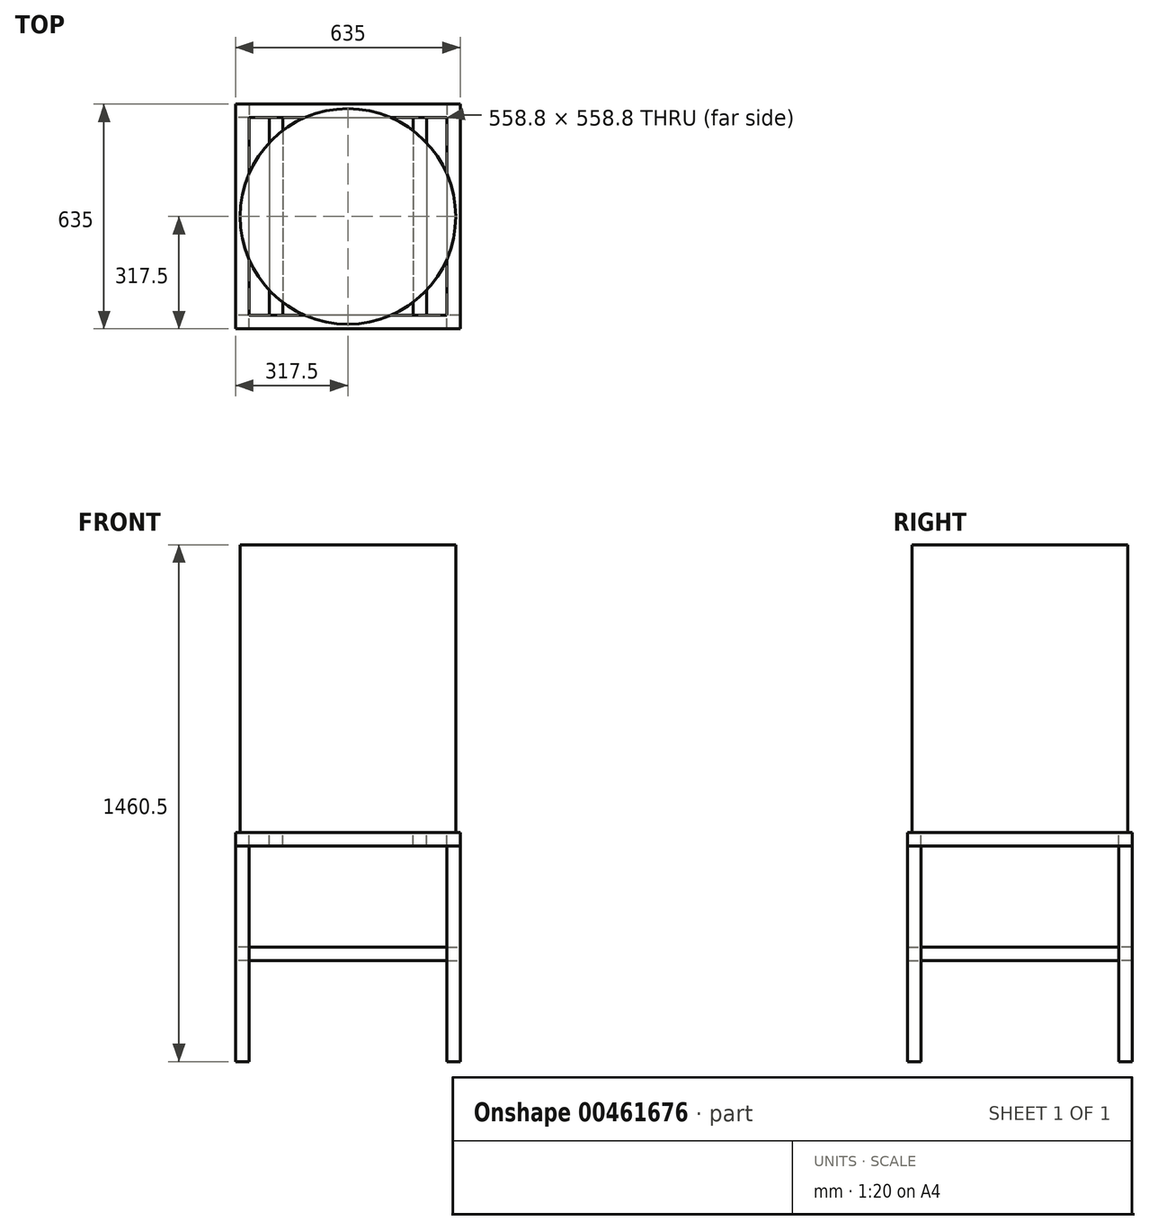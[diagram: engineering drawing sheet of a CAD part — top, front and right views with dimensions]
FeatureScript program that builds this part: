
annotation { "Feature Type Name" : "Feature", "Feature Type Description" : "" }
export const myFeature = defineFeature(function(context is Context, id is Id, definition is map)
    precondition{}
    {
        {
            var Q0;
            Q0=qCreatedBy(makeId("Top.planeOp"),FACE);
            var sketch = newSketch(context, id + "F0", { "sketchPlane" : qUnion([Q0])});
            skLineSegment(sketch, "E0.bottom", {"start": v(298.45, 298.45) * mm, "end": v(-298.45, 298.45) * mm});
            skLineSegment(sketch, "E0.top", {"start": v(298.45, -298.45) * mm, "end": v(-298.45, -298.45) * mm});
            skLineSegment(sketch, "E0.left", {"start": v(298.45, 298.45) * mm, "end": v(298.45, -298.45) * mm});
            skLineSegment(sketch, "E0.right", {"start": v(-298.45, 298.45) * mm, "end": v(-298.45, -298.45) * mm});
            skPoint(sketch, "E0.middle", {"position": v(0, 0) * mm});
            skCircle(sketch, "E1", {"center": v(0, 0) * mm, "radius": 304.8 * mm, "construction": true});
            skSolve(sketch);
        }
        {
            var Q0;
            Q0=sQuery(id+"F0.wireOp",VERTEX,"E0.left.end");
            var Q1;
            Q1=sQuery(id+"F0.wireOp",EDGE,"E0.top");
            cPlane(context, id + "F1", {"entities" : qUnion([Q0, Q1]), "cplaneType" : CPlaneType.LINE_POINT, "offset" : 25.4 * mm, "width" : 152.4 * mm, "height" : 152.4 * mm});
        }
        {
            var Q0;
            Q0=qCreatedBy(id+"F1.planeOp",FACE);
            var sketch = newSketch(context, id + "F2", { "sketchPlane" : qUnion([Q0])});
            skLineSegment(sketch, "E2.bottom", {"start": v(317.5, 19.05) * mm, "end": v(279.4, 19.05) * mm});
            skLineSegment(sketch, "E2.top", {"start": v(317.5, -19.05) * mm, "end": v(279.4, -19.05) * mm});
            skLineSegment(sketch, "E2.left", {"start": v(317.5, 19.05) * mm, "end": v(317.5, -19.05) * mm});
            skLineSegment(sketch, "E2.right", {"start": v(279.4, 19.05) * mm, "end": v(279.4, -19.05) * mm});
            skPoint(sketch, "E2.middle", {"position": v(298.45, 0) * mm});
            skSolve(sketch);
        }
        {
            var Q0;
            Q0=makeQuery(id+"F2.imprint","IMPRINT",FACE,{"disambiguationData":[TD([[makeQuery(id+"F2.imprint","IMPRINT",EDGE,{"derivedFrom":sQuery(id+"F2.wireOp",EDGE,"E2.bottom")}),1.0]])]});
            var Q1;
            Q1=sQuery(id+"F0.wireOp",EDGE,"E0.top");
            var Q2;
            Q2=sQuery(id+"F0.wireOp",EDGE,"E0.right");
            var Q3;
            Q3=sQuery(id+"F0.wireOp",EDGE,"E0.bottom");
            var Q4;
            Q4=sQuery(id+"F0.wireOp",EDGE,"E0.left");
            sweep(context, id + "F3", {"profiles" : qUnion([Q0]), "path" : qUnion([Q1, Q2, Q3, Q4])});
        }
        {
            var Q0;
            Q0=makeQuery(id+"F3.opSweep","SWEPT_FACE",FACE,{"disambiguationData":[OSD([sQuery(id+"F0.wireOp",EDGE,"E0.top"),sQuery(id+"F2.wireOp",EDGE,"E2.left")])]});
            cPlane(context, id + "F4", {"entities" : qUnion([Q0]), "cplaneType" : CPlaneType.OFFSET, "offset" : 19.05 * mm, "oppositeDirection" : true, "width" : 152.4 * mm, "height" : 152.4 * mm});
        }
        {
            var Q0;
            Q0=qCreatedBy(id+"F4.planeOp",FACE);
            var sketch = newSketch(context, id + "F5", { "sketchPlane" : qUnion([Q0])});
            skLineSegment(sketch, "E3", {"start": v(0, 0) * mm, "end": v(0, -240.4) * mm, "construction": true});
            skLineSegment(sketch, "E4", {"start": v(-298.45, -19.05) * mm, "end": v(-298.45, -628.65) * mm});
            skLineSegment(sketch, "E5.MirrorCS", {"start": v(298.45, -19.05) * mm, "end": v(298.45, -628.65) * mm});
            skSolve(sketch);
        }
        {
            var Q0;
            Q0=sQuery(id+"F5.wireOp",VERTEX,"E4.end");
            var Q1;
            Q1=sQuery(id+"F5.wireOp",EDGE,"E4");
            cPlane(context, id + "F6", {"entities" : qUnion([Q0, Q1]), "cplaneType" : CPlaneType.LINE_POINT, "offset" : 25.4 * mm, "width" : 152.4 * mm, "height" : 152.4 * mm});
        }
        {
            var Q0;
            Q0=qCreatedBy(id+"F6.planeOp",FACE);
            var sketch = newSketch(context, id + "F7", { "sketchPlane" : qUnion([Q0])});
            skLineSegment(sketch, "E6.bottom", {"start": v(-317.5, 317.5) * mm, "end": v(-279.4, 317.5) * mm});
            skLineSegment(sketch, "E6.top", {"start": v(-317.5, 279.4) * mm, "end": v(-279.4, 279.4) * mm});
            skLineSegment(sketch, "E6.left", {"start": v(-317.5, 317.5) * mm, "end": v(-317.5, 279.4) * mm});
            skLineSegment(sketch, "E6.right", {"start": v(-279.4, 317.5) * mm, "end": v(-279.4, 279.4) * mm});
            skPoint(sketch, "E6.middle", {"position": v(-298.45, 298.45) * mm});
            skSolve(sketch);
        }
        {
            var Q0;
            Q0=makeQuery(id+"F7.imprint","IMPRINT",FACE,{"disambiguationData":[TD([[makeQuery(id+"F7.imprint","IMPRINT",EDGE,{"derivedFrom":sQuery(id+"F7.wireOp",EDGE,"E6.bottom")}),-1.0]])]});
            var Q1;
            Q1=sQuery(id+"F5.wireOp",EDGE,"E4");
            sweep(context, id + "F8", {"profiles" : qUnion([Q0]), "path" : qUnion([Q1])});
        }
        {
            var Q0;
            Q0=sQuery(id+"F5.wireOp",VERTEX,"E5.MirrorCS.end");
            var Q1;
            Q1=sQuery(id+"F5.wireOp",EDGE,"E5.MirrorCS");
            cPlane(context, id + "F9", {"entities" : qUnion([Q0, Q1]), "cplaneType" : CPlaneType.LINE_POINT, "offset" : 25.4 * mm, "width" : 152.4 * mm, "height" : 152.4 * mm});
        }
        {
            var Q0;
            Q0=qCreatedBy(id+"F9.planeOp",FACE);
            var sketch = newSketch(context, id + "F10", { "sketchPlane" : qUnion([Q0])});
            skLineSegment(sketch, "E7.bottom", {"start": v(279.4, 279.4) * mm, "end": v(317.5, 279.4) * mm});
            skLineSegment(sketch, "E7.top", {"start": v(279.4, 317.5) * mm, "end": v(317.5, 317.5) * mm});
            skLineSegment(sketch, "E7.left", {"start": v(279.4, 279.4) * mm, "end": v(279.4, 317.5) * mm});
            skLineSegment(sketch, "E7.right", {"start": v(317.5, 279.4) * mm, "end": v(317.5, 317.5) * mm});
            skPoint(sketch, "E7.middle", {"position": v(298.45, 298.45) * mm});
            skSolve(sketch);
        }
        {
            var Q0;
            Q0=makeQuery(id+"F8.opSweep","SWEPT_BODY",BODY,{"disambiguationData":[OSD([sQuery(id+"F5.wireOp",EDGE,"E4"),sQuery(id+"F7.wireOp",EDGE,"E6.bottom"),sQuery(id+"F7.wireOp",EDGE,"E6.top"),sQuery(id+"F7.wireOp",EDGE,"E6.left"),sQuery(id+"F7.wireOp",EDGE,"E6.right")])]});
            var Q1;
            Q1=qCreatedBy(makeId("Right.planeOp"),FACE);
            mirror(context, id + "F11", {"entities" : qUnion([Q0]), "mirrorPlane" : qUnion([Q1])});
        }
        {
            var Q0;
            Q0=makeQuery(id+"F8.opSweep","SWEPT_BODY",BODY,{"disambiguationData":[OSD([sQuery(id+"F5.wireOp",EDGE,"E4"),sQuery(id+"F7.wireOp",EDGE,"E6.bottom"),sQuery(id+"F7.wireOp",EDGE,"E6.top"),sQuery(id+"F7.wireOp",EDGE,"E6.left"),sQuery(id+"F7.wireOp",EDGE,"E6.right")])]});
            var Q1;
            Q1=makeQuery(id+"F11.opPattern","COPY",BODY,{"derivedFrom":makeQuery(id+"F8.opSweep","SWEPT_BODY",BODY,{"disambiguationData":[OSD([sQuery(id+"F5.wireOp",EDGE,"E4"),sQuery(id+"F7.wireOp",EDGE,"E6.bottom"),sQuery(id+"F7.wireOp",EDGE,"E6.top"),sQuery(id+"F7.wireOp",EDGE,"E6.left"),sQuery(id+"F7.wireOp",EDGE,"E6.right")])]}),"instanceName":"1"});
            var Q2;
            Q2=qCreatedBy(makeId("Front.planeOp"),FACE);
            mirror(context, id + "F12", {"entities" : qUnion([Q0, Q1]), "mirrorPlane" : qUnion([Q2])});
        }
        {
            var Q0;
            Q0=qCreatedBy(id+"F4.planeOp",FACE);
            var sketch = newSketch(context, id + "F13", { "sketchPlane" : qUnion([Q0])});
            skLineSegment(sketch, "E8", {"start": v(-279.4, -323.85) * mm, "end": v(279.4, -323.85) * mm});
            skSolve(sketch);
        }
        {
            var Q0;
            Q0=makeQuery(id+"F11.opPattern","COPY",FACE,{"derivedFrom":makeQuery(id+"F8.opSweep","SWEPT_FACE",FACE,{"disambiguationData":[OSD([sQuery(id+"F5.wireOp",EDGE,"E4"),sQuery(id+"F7.wireOp",EDGE,"E6.right")])]}),"instanceName":"1"});
            var sketch = newSketch(context, id + "F14", { "sketchPlane" : qUnion([Q0])});
            skLineSegment(sketch, "E9.bottom", {"start": v(317.5, -342.9) * mm, "end": v(279.4, -342.9) * mm});
            skLineSegment(sketch, "E9.top", {"start": v(317.5, -304.8) * mm, "end": v(279.4, -304.8) * mm});
            skLineSegment(sketch, "E9.left", {"start": v(317.5, -342.9) * mm, "end": v(317.5, -304.8) * mm});
            skLineSegment(sketch, "E9.right", {"start": v(279.4, -342.9) * mm, "end": v(279.4, -304.8) * mm});
            skPoint(sketch, "E9.middle", {"position": v(298.45, -323.85) * mm});
            skSolve(sketch);
        }
        {
            var Q0;
            Q0=makeQuery(id+"F14.imprint","IMPRINT",FACE,{"disambiguationData":[TD([[makeQuery(id+"F14.imprint","IMPRINT",EDGE,{"derivedFrom":sQuery(id+"F14.wireOp",EDGE,"E9.bottom")}),-1.0]])]});
            var Q1;
            Q1=sQuery(id+"F13.wireOp",EDGE,"E8");
            sweep(context, id + "F15", {"profiles" : qUnion([Q0]), "path" : qUnion([Q1])});
        }
        {
            var Q0;
            Q0=makeQuery(id+"F15.opSweep","SWEPT_BODY",BODY,{"disambiguationData":[OSD([sQuery(id+"F13.wireOp",EDGE,"E8"),sQuery(id+"F14.wireOp",EDGE,"E9.bottom"),sQuery(id+"F14.wireOp",EDGE,"E9.top"),sQuery(id+"F14.wireOp",EDGE,"E9.left"),sQuery(id+"F14.wireOp",EDGE,"E9.right")])]});
            var Q1;
            Q1=qCreatedBy(makeId("Front.planeOp"),FACE);
            mirror(context, id + "F16", {"entities" : qUnion([Q0]), "mirrorPlane" : qUnion([Q1])});
        }
        {
            var Q0;
            Q0=makeQuery(id+"F3.opSweep","SWEPT_FACE",FACE,{"disambiguationData":[OSD([sQuery(id+"F0.wireOp",EDGE,"E0.left"),sQuery(id+"F2.wireOp",EDGE,"E2.left")])]});
            cPlane(context, id + "F17", {"entities" : qUnion([Q0]), "cplaneType" : CPlaneType.OFFSET, "offset" : 19.05 * mm, "oppositeDirection" : true, "width" : 152.4 * mm, "height" : 152.4 * mm});
        }
        {
            var Q0;
            Q0=qCreatedBy(id+"F17.planeOp",FACE);
            var sketch = newSketch(context, id + "F18", { "sketchPlane" : qUnion([Q0])});
            skLineSegment(sketch, "E10", {"start": v(-279.4, -323.85) * mm, "end": v(279.4, -323.85) * mm});
            skSolve(sketch);
        }
        {
            var Q0;
            Q0=makeQuery(id+"F11.opPattern","COPY",FACE,{"derivedFrom":makeQuery(id+"F8.opSweep","SWEPT_FACE",FACE,{"disambiguationData":[OSD([sQuery(id+"F5.wireOp",EDGE,"E4"),sQuery(id+"F7.wireOp",EDGE,"E6.top")])]}),"instanceName":"1"});
            var sketch = newSketch(context, id + "F19", { "sketchPlane" : qUnion([Q0])});
            skLineSegment(sketch, "E11.bottom", {"start": v(-279.4, -342.9) * mm, "end": v(-317.5, -342.9) * mm});
            skLineSegment(sketch, "E11.top", {"start": v(-279.4, -304.8) * mm, "end": v(-317.5, -304.8) * mm});
            skLineSegment(sketch, "E11.left", {"start": v(-279.4, -342.9) * mm, "end": v(-279.4, -304.8) * mm});
            skLineSegment(sketch, "E11.right", {"start": v(-317.5, -342.9) * mm, "end": v(-317.5, -304.8) * mm});
            skPoint(sketch, "E11.middle", {"position": v(-298.45, -323.85) * mm});
            skSolve(sketch);
        }
        {
            var Q0;
            Q0 = qSketchRegion(id + "F19", true);
            var Q1;
            Q1=sQuery(id+"F18.wireOp",EDGE,"E10");
            sweep(context, id + "F20", {"profiles" : qUnion([Q0]), "path" : qUnion([Q1])});
        }
        {
            var Q0;
            Q0=makeQuery(id+"F20.opSweep","SWEPT_BODY",BODY,{"disambiguationData":[OSD([sQuery(id+"F18.wireOp",EDGE,"E10"),sQuery(id+"F19.wireOp",EDGE,"E11.bottom"),sQuery(id+"F19.wireOp",EDGE,"E11.top"),sQuery(id+"F19.wireOp",EDGE,"E11.left"),sQuery(id+"F19.wireOp",EDGE,"E11.right")])]});
            var Q1;
            Q1=qCreatedBy(makeId("Right.planeOp"),FACE);
            mirror(context, id + "F21", {"entities" : qUnion([Q0]), "mirrorPlane" : qUnion([Q1])});
        }
        {
            var Q0;
            Q0=qCreatedBy(makeId("Top.planeOp"),FACE);
            var sketch = newSketch(context, id + "F22", { "sketchPlane" : qUnion([Q0])});
            skLineSegment(sketch, "E12", {"start": v(-203.2, 279.4) * mm, "end": v(-203.2, -279.4) * mm});
            skSolve(sketch);
        }
        {
            var Q0;
            Q0=makeQuery(id+"F3.opSweep","SWEPT_FACE",FACE,{"disambiguationData":[OSD([sQuery(id+"F0.wireOp",EDGE,"E0.bottom"),sQuery(id+"F2.wireOp",EDGE,"E2.right")])]});
            var sketch = newSketch(context, id + "F23", { "sketchPlane" : qUnion([Q0])});
            skLineSegment(sketch, "E13.bottom", {"start": v(-184.15, -19.05) * mm, "end": v(-222.25, -19.05) * mm});
            skLineSegment(sketch, "E13.top", {"start": v(-184.15, 19.05) * mm, "end": v(-222.25, 19.05) * mm});
            skLineSegment(sketch, "E13.left", {"start": v(-184.15, -19.05) * mm, "end": v(-184.15, 19.05) * mm});
            skLineSegment(sketch, "E13.right", {"start": v(-222.25, -19.05) * mm, "end": v(-222.25, 19.05) * mm});
            skPoint(sketch, "E13.middle", {"position": v(-203.2, 0) * mm});
            skSolve(sketch);
        }
        {
            var Q0;
            Q0 = qSketchRegion(id + "F23", true);
            var Q1;
            Q1=sQuery(id+"F22.wireOp",EDGE,"E12");
            sweep(context, id + "F24", {"profiles" : qUnion([Q0]), "path" : qUnion([Q1])});
        }
        {
            var Q0;
            Q0=makeQuery(id+"F24.opSweep","SWEPT_BODY",BODY,{"disambiguationData":[OSD([sQuery(id+"F22.wireOp",EDGE,"E12"),sQuery(id+"F23.wireOp",EDGE,"E13.bottom"),sQuery(id+"F23.wireOp",EDGE,"E13.top"),sQuery(id+"F23.wireOp",EDGE,"E13.left"),sQuery(id+"F23.wireOp",EDGE,"E13.right")])]});
            var Q1;
            Q1=qCreatedBy(makeId("Right.planeOp"),FACE);
            mirror(context, id + "F25", {"entities" : qUnion([Q0]), "mirrorPlane" : qUnion([Q1])});
        }
        {
            var Q0;
            Q0=makeQuery(id+"F3.opSweep","SWEPT_FACE",FACE,{"disambiguationData":[OSD([sQuery(id+"F0.wireOp",EDGE,"E0.top"),sQuery(id+"F2.wireOp",EDGE,"E2.bottom")])]});
            var sketch = newSketch(context, id + "F26", { "sketchPlane" : qUnion([Q0])});
            skCircle(sketch, "E14", {"center": v(0, 0) * mm, "radius": 304.8 * mm});
            skSolve(sketch);
        }
        {
            var Q0;
            Q0 = qSketchRegion(id + "F26", true);
            extrude(context, id + "F27", {"entities" : qUnion([Q0]), "depth" : 812.8 * mm});
        }
    });
